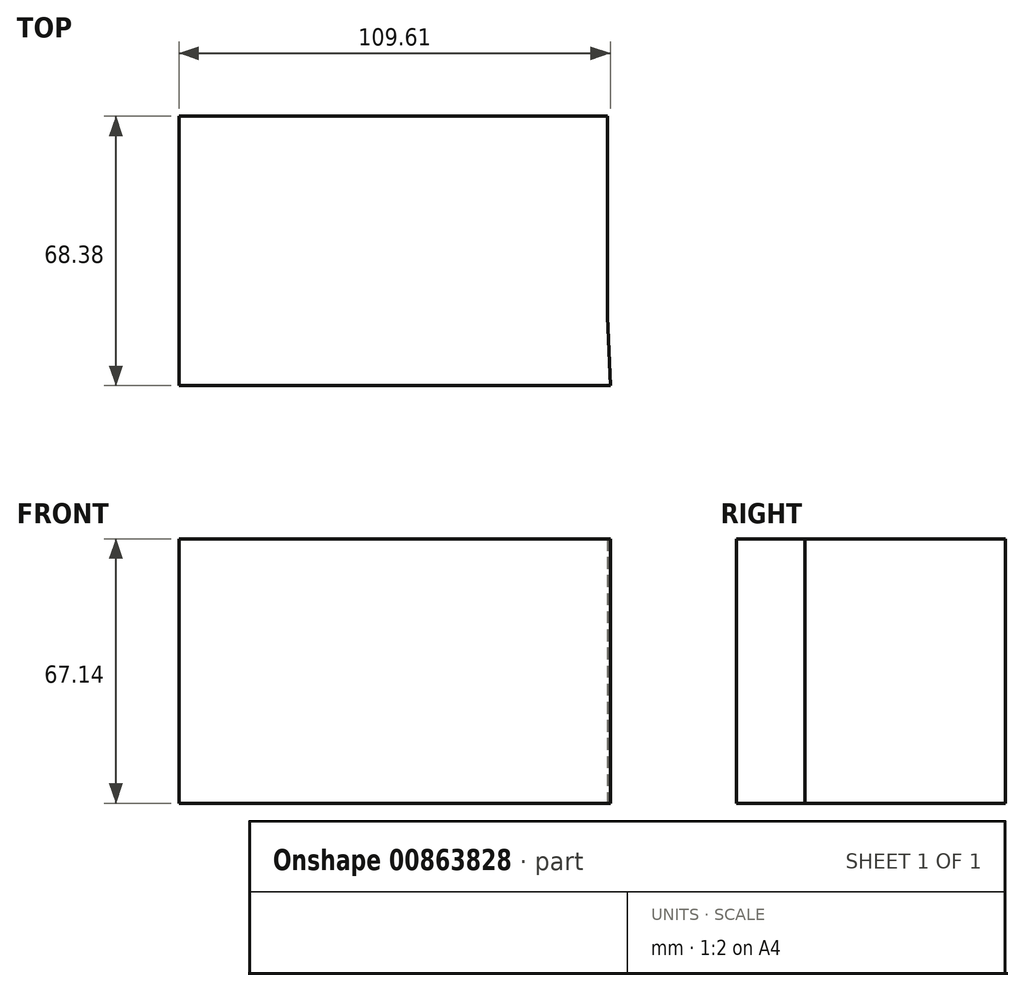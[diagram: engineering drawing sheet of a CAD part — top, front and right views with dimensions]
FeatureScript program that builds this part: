
annotation { "Feature Type Name" : "Feature", "Feature Type Description" : "" }
export const myFeature = defineFeature(function(context is Context, id is Id, definition is map)
    precondition{}
    {
        {
            var Q0;
            Q0=qCreatedBy(makeId("Top.planeOp"),FACE);
            var sketch = newSketch(context, id + "F0", { "sketchPlane" : qUnion([Q0])});
            skLineSegment(sketch, "E0", {"start": v(50.74, 0) * mm, "end": v(50.74, 50.9) * mm});
            skLineSegment(sketch, "E1", {"start": v(50.74, 50.9) * mm, "end": v(-58.16, 50.9) * mm});
            skLineSegment(sketch, "E2", {"start": v(-58.16, 50.9) * mm, "end": v(-58.16, -17.49) * mm});
            skLineSegment(sketch, "E3", {"start": v(-58.16, -17.49) * mm, "end": v(51.45, -17.49) * mm});
            skLineSegment(sketch, "E4", {"start": v(51.45, -17.49) * mm, "end": v(50.74, 0) * mm});
            skSolve(sketch);
        }
        {
            var Q0;
            Q0=makeQuery(id+"F0.imprint","IMPRINT",FACE,{"disambiguationData":[TD([[makeQuery(id+"F0.imprint","IMPRINT",EDGE,{"derivedFrom":sQuery(id+"F0.wireOp",EDGE,"E0")}),1.0]])]});
            extrude(context, id + "F1", {"entities" : qUnion([Q0]), "depth" : 67.14 * mm, "offsetDistance" : 25.4 * mm});
        }
    });
